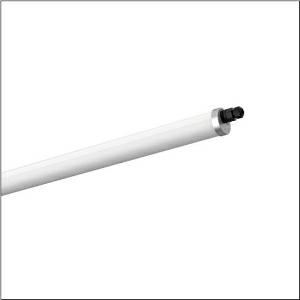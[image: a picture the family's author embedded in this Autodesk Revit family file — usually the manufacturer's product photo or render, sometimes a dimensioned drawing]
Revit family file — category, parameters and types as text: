
# Revit family: monsun_31_tube_51ft107n480a
name_source: partatom
category: Lighting Fixtures
units: mm (PartAtom-declared; Revit-internal decimal feet)

## family parameters
Cut with Voids When Loaded = No
Host = Face
Light Source = No
Part Type = Normal
Room Calculation Point = No
Round Connector Dimension = Use Diameter
Shared = No

## types (1)
- Monsun 31 Tube (1 x LED, 8000 lm, 50 W, 4000K)
    Apparent Load = 50 VA
    CIE Flux Codes = 42 71 89 91 100
    Color Rendering = 80
    Color Temperature = 4000K
    Default Elevation = 1800 mm
    Description = Monsun 31 Tube, tubular luminaire, primary optical cover: diffuser, of PMMA, light emission: direct distribution, primary light characteristic: symmetric, installation type: suspended mounting, surface-mounted, LED, rated luminous flux: 8.000lm, luminous efficacy: 160lm/W, light colour: 840, colour temperature: 4000K, control gear: ON/OFF, with with 1 terminal, 3-pole, max. 2.5mm², through-wiring: 3x 1.5mm², mains connection: 220..240V, AC, 50/60Hz, rated input power: 50W, housing, cylindrical, of PMMA, semi-transparent, matt white, with luminaire and ceiling fastening, V4A, mounting with brackets of stainless steel, length: 1.560mm, diameter: 75mm, end cap, of stainless steel (V4A), protection rating (complete): IP67/IP69K, insulation class (complete): insulation class I (protective earthing), certification: CE, UKCA, impact resistance: IK07, permissible operating ambient temperature: -20..+40°C, corresponds to IFS (International Featured Standards) requirements for safety and quality in the food industry, usage in unprotected outdoor areas possible with horizontal mounting, contact your sales advisor before using the luminaires in applications with unclear chemical exposure, large temperature fluctuations or condensation-forming humidity, packaging unit: 1 piece
    Height = 83 mm
    Lamp = 1 x LED
    Lamp Light Flux = 8000 lm
    Lamp Power = 50 W
    Lamp count = 1
    Length = 1560 mm
    Luminous efficacy = 160 lm/W
    Manufacturer = Siteco
    ModVariant = No
    Model = 51FT107N480A
    Mounting Place = Ceiling
    Mounting Type = Pendant
    Number of Poles = 1
    OnlyDefault = Yes
    Power Factor = 1
    Product Name = Monsun 31 Tube
    Product group = tubular luminaire
    ProductGroupID = 906
    Protection Class = Protection class I
    RLX_Detail_Level = 1
    RLX_Emergency_Light_Flux = 0 lm
    RLX_Emergency_Type = 0
    RLX_Emergency_Type_DB = No
    RlxData = <blob elided: 25397 chars, md5=eb335d5f>
    Socket = socket
    Standby Power = 0 W
    System Light Flux = 8000 lm
    System Power = 50 W
    Type Comments = Product without accessories
    Type Image = l_1228461.jpg
    URL = http://relux.com
    VarID = ---
    Voltage = 0 V
    Weight = 0.00 kg
    Width = 75 mm

## geometry (parser evidence)
native form markers: Blend x4, Sweep x13
no freeform markers — native parametric forms only
